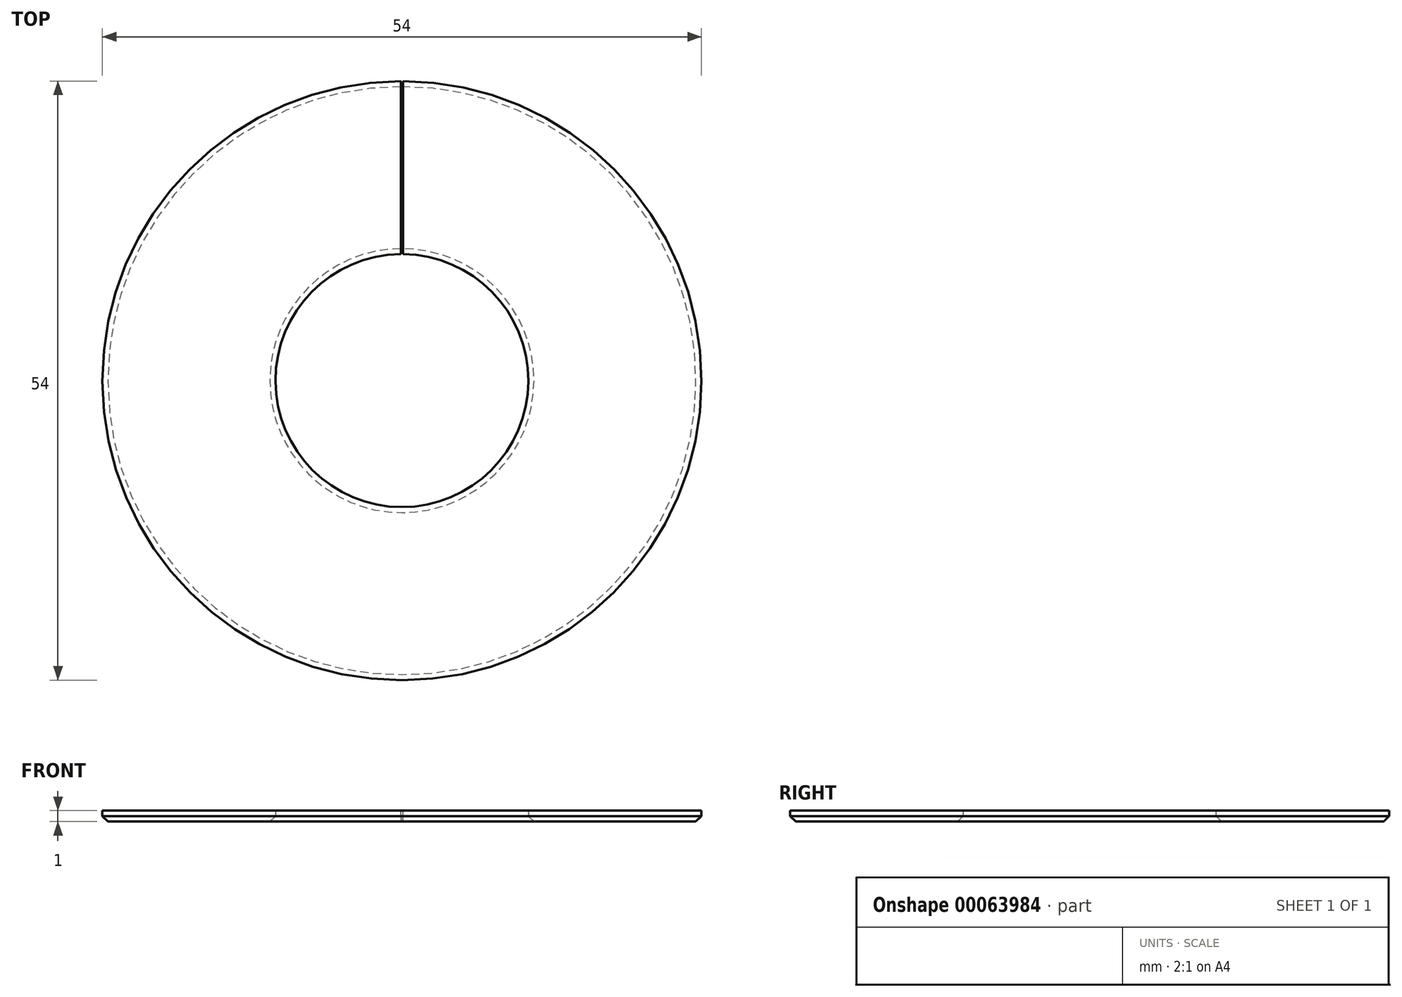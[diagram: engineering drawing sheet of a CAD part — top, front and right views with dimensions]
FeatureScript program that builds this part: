
annotation { "Feature Type Name" : "Feature", "Feature Type Description" : "" }
export const myFeature = defineFeature(function(context is Context, id is Id, definition is map)
    precondition{}
    {
        {
            var Q0;
            Q0=qCreatedBy(makeId("Top.planeOp"),FACE);
            var sketch = newSketch(context, id + "F0", { "sketchPlane" : qUnion([Q0])});
            skCircle(sketch, "E0", {"center": v(0, 0) * mm, "radius": 27 * mm});
            skCircle(sketch, "E1", {"center": v(0, 0) * mm, "radius": 11.4 * mm});
            skSolve(sketch);
        }
        {
            var Q0;
            Q0 = qSketchRegion(id + "F0", true);
            extrude(context, id + "F1", {"entities" : qUnion([Q0]), "depth" : 1 * mm, "offsetDistance" : 25 * mm});
        }
        {
            var Q0;
            Q0=makeQuery(id+"F1.opExtrude","CAP_FACE",FACE,{"disambiguationData":[OSD([sQuery(id+"F0.wireOp",EDGE,"E0"),sQuery(id+"F0.wireOp",EDGE,"E1")])],"isStart":false});
            var sketch = newSketch(context, id + "F2", { "sketchPlane" : qUnion([Q0])});
            skLineSegment(sketch, "E2", {"start": v(-0.1, 27) * mm, "end": v(-0.1, 11.4) * mm});
            skLineSegment(sketch, "E3", {"start": v(-0.1, 11.4) * mm, "end": v(0.1, 11.4) * mm});
            skLineSegment(sketch, "E4", {"start": v(0.1, 11.4) * mm, "end": v(0.1, 27) * mm});
            skArc(sketch, "E5.0", {"start": v(0.1, 27) * mm, "mid": v(0, 27) * mm, "end": v(-0.1, 27) * mm});
            skSolve(sketch);
        }
        {
            var Q0;
            Q0 = qSketchRegion(id + "F2", true);
            var Q1;
            Q1=makeQuery(id+"F1.opExtrude","CAP_FACE",FACE,{"disambiguationData":[OSD([sQuery(id+"F0.wireOp",EDGE,"E0"),sQuery(id+"F0.wireOp",EDGE,"E1")])],"isStart":true});
            extrude(context, id + "F3", {"entities" : qUnion([Q0]), "operationType" : NewBodyOperationType.REMOVE, "endBound" : BoundingType.UP_TO_SURFACE, "oppositeDirection" : true, "depth" : 25 * mm, "endBoundEntityFace" : qUnion([Q1]), "offsetDistance" : 25 * mm});
        }
        {
            var Q0;
            Q0=makeQuery(id+"F1.opExtrude","CAP_EDGE",EDGE,{"disambiguationData":[OSD([sQuery(id+"F0.wireOp",EDGE,"E0")])],"isStart":true});
            var Q1;
            Q1=makeQuery(id+"F1.opExtrude","CAP_EDGE",EDGE,{"disambiguationData":[OSD([sQuery(id+"F0.wireOp",EDGE,"E1")])],"isStart":true});
            chamfer(context, id + "F4", {"entities" : qUnion([Q0, Q1]), "width" : 0.5 * mm, "tangentPropagation" : true});
        }
    });
